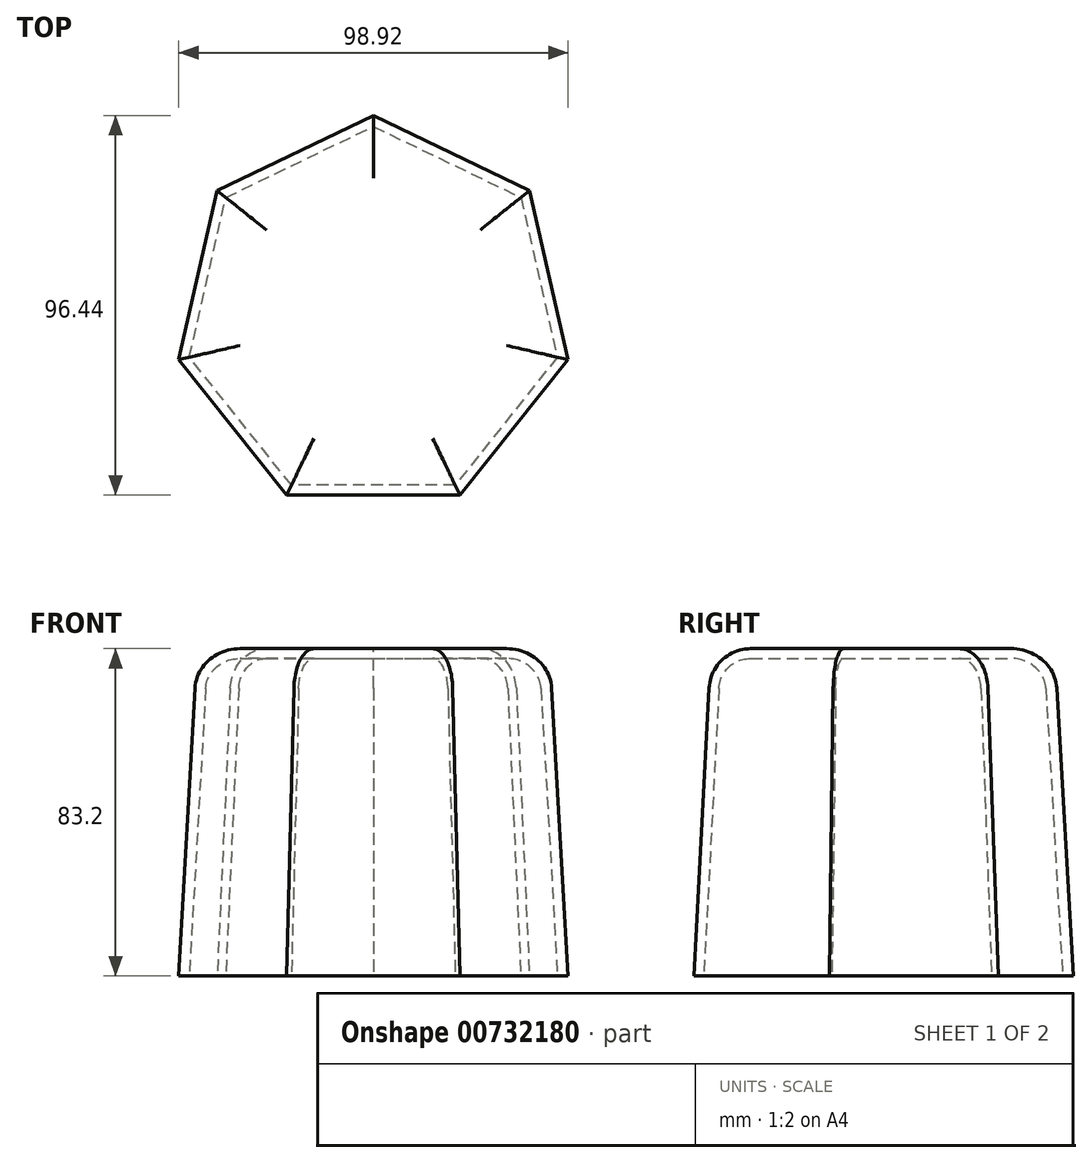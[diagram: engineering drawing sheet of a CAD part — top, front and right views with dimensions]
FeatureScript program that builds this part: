
annotation { "Feature Type Name" : "Feature", "Feature Type Description" : "" }
export const myFeature = defineFeature(function(context is Context, id is Id, definition is map)
    precondition{}
    {
        {
            var Q0;
            Q0=qCreatedBy(makeId("Top.planeOp"),FACE);
            var sketch = newSketch(context, id + "F0", { "sketchPlane" : qUnion([Q0])});
            skCircle(sketch, "E0.cCircle", {"center": v(0, 0) * mm, "radius": 42.66 * mm, "construction": true});
            skLineSegment(sketch, "E0.0", {"start": v(20.54, -42.66) * mm, "end": v(-20.54, -42.66) * mm});
            skLineSegment(sketch, "E0.1", {"start": v(-20.54, -42.66) * mm, "end": v(-46.16, -10.54) * mm});
            skLineSegment(sketch, "E0.2", {"start": v(-46.16, -10.54) * mm, "end": v(-37.02, 29.52) * mm});
            skLineSegment(sketch, "E0.3", {"start": v(-37.02, 29.52) * mm, "end": v(0, 47.34) * mm});
            skLineSegment(sketch, "E0.4", {"start": v(0, 47.34) * mm, "end": v(37.02, 29.52) * mm});
            skLineSegment(sketch, "E0.5", {"start": v(37.02, 29.52) * mm, "end": v(46.16, -10.54) * mm});
            skLineSegment(sketch, "E0.6", {"start": v(46.16, -10.54) * mm, "end": v(20.54, -42.66) * mm});
            skPoint(sketch, "E0.0.midPoint", {"position": v(0, -42.66) * mm});
            skSolve(sketch);
        }
        {
            var Q0;
            Q0=makeQuery(id+"F0.imprint","IMPRINT",FACE,{"disambiguationData":[TD([[makeQuery(id+"F0.imprint","IMPRINT",EDGE,{"derivedFrom":sQuery(id+"F0.wireOp",EDGE,"E0.0")}),-1.0]])]});
            extrude(context, id + "F1", {"entities" : qUnion([Q0]), "depth" : 25 * mm, "offsetDistance" : 25 * mm, "hasDraft" : true, "draftAngle" : 3 * degree, "draftPullDirection" : true, "hasSecondDirection" : true, "secondDirectionOppositeDirection" : true, "secondDirectionDepth" : 58.2 * mm, "hasSecondDirectionDraft" : true, "secondDirectionDraftAngle" : 3 * degree});
        }
        {
            var Q0;
            Q0=makeQuery(id+"F1.opExtrude","CAP_EDGE",EDGE,{"disambiguationData":[OSD([sQuery(id+"F0.wireOp",EDGE,"E0.2")])],"isStart":false});
            var Q1;
            Q1=makeQuery(id+"F1.opExtrude","CAP_EDGE",EDGE,{"disambiguationData":[OSD([sQuery(id+"F0.wireOp",EDGE,"E0.3")])],"isStart":false});
            var Q2;
            Q2=makeQuery(id+"F1.opExtrude","CAP_FACE",FACE,{"disambiguationData":[OSD([sQuery(id+"F0.wireOp",EDGE,"E0.0"),sQuery(id+"F0.wireOp",EDGE,"E0.1"),sQuery(id+"F0.wireOp",EDGE,"E0.2"),sQuery(id+"F0.wireOp",EDGE,"E0.3"),sQuery(id+"F0.wireOp",EDGE,"E0.4"),sQuery(id+"F0.wireOp",EDGE,"E0.5"),sQuery(id+"F0.wireOp",EDGE,"E0.6")])],"isStart":false});
            fillet(context, id + "F2", {"entities" : qUnion([Q0, Q1, Q2]), "radius" : 10.57 * mm, "tangentPropagation" : true, "allowEdgeOverflow" : false});
        }
        {
            var Q0;
            Q0=makeQuery(id+"F1.opExtrude","CAP_FACE",FACE,{"disambiguationData":[OSD([sQuery(id+"F0.wireOp",EDGE,"E0.0"),sQuery(id+"F0.wireOp",EDGE,"E0.1"),sQuery(id+"F0.wireOp",EDGE,"E0.2"),sQuery(id+"F0.wireOp",EDGE,"E0.3"),sQuery(id+"F0.wireOp",EDGE,"E0.4"),sQuery(id+"F0.wireOp",EDGE,"E0.5"),sQuery(id+"F0.wireOp",EDGE,"E0.6")])],"isStart":true});
            shell(context, id + "F3", {"entities" : qUnion([Q0]), "thickness" : 2.5 * mm});
        }
        {
            var Q0;
            Q0=makeQuery(id+"F1.opExtrude","CAP_EDGE",EDGE,{"disambiguationData":[OSD([sQuery(id+"F0.wireOp",EDGE,"E0.2")])],"isStart":true});
            cPoint(context, id + "F4", {"entities" : qUnion([Q0]), "parameter" : 0.5});
        }
        {
            var Q0;
            {var subQ0=sQuery(id+"F0.wireOp",EDGE,"E0.2");Q0=makeQuery(id+"F3.opShell","OFFSET_EDGE",EDGE,{"disambiguationData":[OSD([subQ0]),TDD([makeQuery(id+"F1.opExtrude","CAP_EDGE",EDGE,{"disambiguationData":[OSD([subQ0])],"isStart":true})])]});}
            cPoint(context, id + "F5", {"entities" : qUnion([Q0]), "parameter" : 0.5});
        }
        {
            var Q0;
            {var subQ0=sQuery(id+"F0.wireOp",EDGE,"E0.2");var subQ1=makeQuery(id+"F1.opExtrude","SWEPT_FACE",FACE,{"disambiguationData":[OSD([subQ0])]});Q0=makeQuery(id+"F2.opFillet","BLEND_EDGE",EDGE,{"blendedFrom":[makeQuery(id+"F1.opExtrude","CAP_EDGE",EDGE,{"disambiguationData":[OSD([subQ0])],"isStart":false}),makeQuery(id+"F1.*.booleanUnion.opBoolean","MERGE",FACE,{"derivedFrom":[makeQuery(id+"F1.*.split.splitOp","SPLIT",FACE,{"derivedFrom":subQ1}),makeQuery(id+"F1.*.split.splitOp","SPLIT",FACE,{"derivedFrom":subQ1,"isFromBackBody":true})]})],"blendedInto":[makeQuery(id+"F1.*.booleanUnion.opBoolean","MERGE",FACE,{"derivedFrom":[makeQuery(id+"F1.*.split.splitOp","SPLIT",FACE,{"derivedFrom":subQ1}),makeQuery(id+"F1.*.split.splitOp","SPLIT",FACE,{"derivedFrom":subQ1,"isFromBackBody":true})]})]});}
            cPoint(context, id + "F6", {"entities" : qUnion([Q0]), "parameter" : 0.5});
        }
        {
            var Q0;
            Q0 = qCreatedBy(id + "F4" ,VERTEX);
            var Q1;
            Q1 = qCreatedBy(id + "F5" ,VERTEX);
            var Q2;
            Q2 = qCreatedBy(id + "F6" ,VERTEX);
            cPlane(context, id + "F7", {"entities" : qUnion([Q0, Q1, Q2]), "cplaneType" : CPlaneType.THREE_POINT, "offset" : 25 * mm, "width" : 150 * mm, "height" : 150 * mm});
        }
    });
